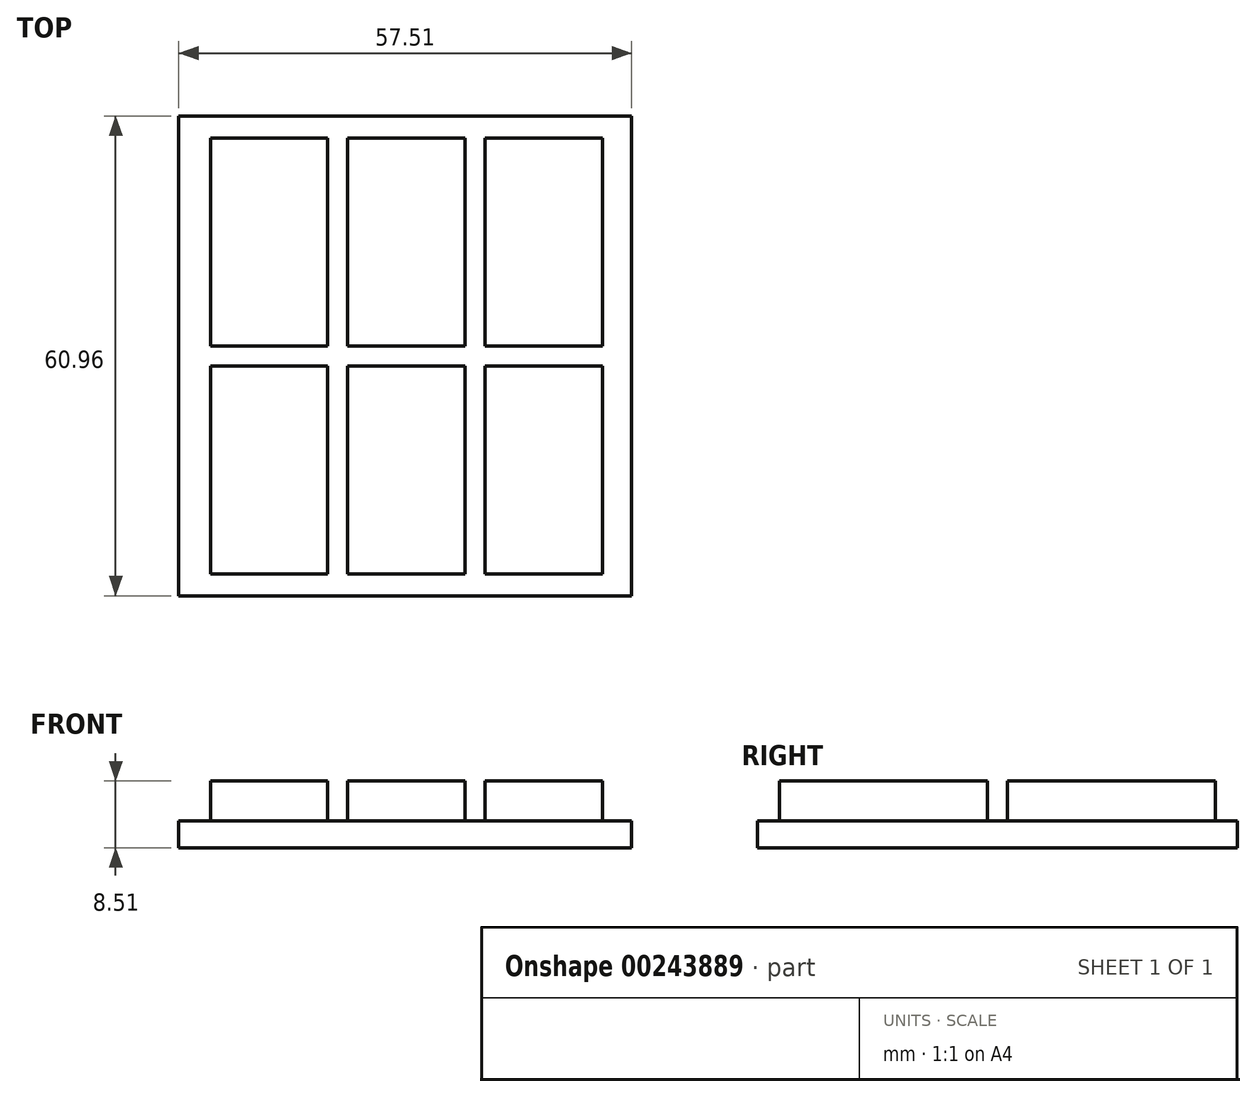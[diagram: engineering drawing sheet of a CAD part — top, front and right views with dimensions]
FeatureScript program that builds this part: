
annotation { "Feature Type Name" : "Feature", "Feature Type Description" : "" }
export const myFeature = defineFeature(function(context is Context, id is Id, definition is map)
    precondition{}
    {
        {
            var Q0;
            Q0=qCreatedBy(makeId("Top.planeOp"),FACE);
            var sketch = newSketch(context, id + "F0", { "sketchPlane" : qUnion([Q0])});
            skLineSegment(sketch, "E0.bottom", {"start": v(-24.89, 27.69) * mm, "end": v(-9.99, 27.69) * mm});
            skLineSegment(sketch, "E0.top", {"start": v(-24.89, 1.27) * mm, "end": v(-9.99, 1.27) * mm});
            skLineSegment(sketch, "E0.left", {"start": v(-24.89, 27.69) * mm, "end": v(-24.89, 1.27) * mm});
            skLineSegment(sketch, "E0.right", {"start": v(-9.99, 27.69) * mm, "end": v(-9.99, 1.27) * mm});
            skLineSegment(sketch, "E1.0.1.0", {"start": v(-9.99, -1.27) * mm, "end": v(-9.99, -27.69) * mm});
            skLineSegment(sketch, "E1.0.1.1", {"start": v(-24.89, -1.27) * mm, "end": v(-24.89, -27.69) * mm});
            skLineSegment(sketch, "E1.0.1.2", {"start": v(-24.89, -27.69) * mm, "end": v(-9.99, -27.69) * mm});
            skLineSegment(sketch, "E1.0.1.3", {"start": v(-24.89, -1.27) * mm, "end": v(-9.99, -1.27) * mm});
            skLineSegment(sketch, "E1.1.0.0", {"start": v(7.45, 27.69) * mm, "end": v(7.45, 1.27) * mm});
            skLineSegment(sketch, "E1.1.0.1", {"start": v(-7.45, 27.69) * mm, "end": v(-7.45, 1.27) * mm});
            skLineSegment(sketch, "E1.1.0.2", {"start": v(-7.45, 1.27) * mm, "end": v(7.45, 1.27) * mm});
            skLineSegment(sketch, "E1.1.0.3", {"start": v(-7.45, 27.69) * mm, "end": v(7.45, 27.69) * mm});
            skLineSegment(sketch, "E1.1.1.0", {"start": v(7.45, -1.27) * mm, "end": v(7.45, -27.69) * mm});
            skLineSegment(sketch, "E1.1.1.1", {"start": v(-7.45, -1.27) * mm, "end": v(-7.45, -27.69) * mm});
            skLineSegment(sketch, "E1.1.1.2", {"start": v(-7.45, -27.69) * mm, "end": v(7.45, -27.69) * mm});
            skLineSegment(sketch, "E1.1.1.3", {"start": v(-7.45, -1.27) * mm, "end": v(7.45, -1.27) * mm});
            skLineSegment(sketch, "E1.2.0.0", {"start": v(24.89, 27.69) * mm, "end": v(24.89, 1.27) * mm});
            skLineSegment(sketch, "E1.2.0.1", {"start": v(9.99, 27.69) * mm, "end": v(9.99, 1.27) * mm});
            skLineSegment(sketch, "E1.2.0.2", {"start": v(9.99, 1.27) * mm, "end": v(24.89, 1.27) * mm});
            skLineSegment(sketch, "E1.2.0.3", {"start": v(9.99, 27.69) * mm, "end": v(24.89, 27.69) * mm});
            skLineSegment(sketch, "E1.2.1.0", {"start": v(24.89, -1.27) * mm, "end": v(24.89, -27.69) * mm});
            skLineSegment(sketch, "E1.2.1.1", {"start": v(9.99, -1.27) * mm, "end": v(9.99, -27.69) * mm});
            skLineSegment(sketch, "E1.2.1.2", {"start": v(9.99, -27.69) * mm, "end": v(24.89, -27.69) * mm});
            skLineSegment(sketch, "E1.2.1.3", {"start": v(9.99, -1.27) * mm, "end": v(24.89, -1.27) * mm});
            skLineSegment(sketch, "E1.direction1", {"start": v(-24.89, 1.27) * mm, "end": v(-7.45, 1.27) * mm, "construction": true});
            skLineSegment(sketch, "E1.direction2", {"start": v(-24.89, 1.27) * mm, "end": v(-24.89, -27.69) * mm, "construction": true});
            skSolve(sketch);
        }
        {
            var Q0;
            Q0=makeQuery(id+"F0.imprint","IMPRINT",FACE,{"disambiguationData":[TD([[makeQuery(id+"F0.imprint","IMPRINT",EDGE,{"derivedFrom":sQuery(id+"F0.wireOp",EDGE,"E0.bottom")}),-1.0]])]});
            var Q1;
            Q1=makeQuery(id+"F0.imprint","IMPRINT",FACE,{"disambiguationData":[TD([[makeQuery(id+"F0.imprint","IMPRINT",EDGE,{"derivedFrom":sQuery(id+"F0.wireOp",EDGE,"E1.1.0.0")}),-1.0]])]});
            var Q2;
            Q2=makeQuery(id+"F0.imprint","IMPRINT",FACE,{"disambiguationData":[TD([[makeQuery(id+"F0.imprint","IMPRINT",EDGE,{"derivedFrom":sQuery(id+"F0.wireOp",EDGE,"E1.2.0.0")}),-1.0]])]});
            var Q3;
            Q3=makeQuery(id+"F0.imprint","IMPRINT",FACE,{"disambiguationData":[TD([[makeQuery(id+"F0.imprint","IMPRINT",EDGE,{"derivedFrom":sQuery(id+"F0.wireOp",EDGE,"E1.2.1.0")}),-1.0]])]});
            var Q4;
            Q4=makeQuery(id+"F0.imprint","IMPRINT",FACE,{"disambiguationData":[TD([[makeQuery(id+"F0.imprint","IMPRINT",EDGE,{"derivedFrom":sQuery(id+"F0.wireOp",EDGE,"E1.1.1.0")}),-1.0]])]});
            var Q5;
            Q5=makeQuery(id+"F0.imprint","IMPRINT",FACE,{"disambiguationData":[TD([[makeQuery(id+"F0.imprint","IMPRINT",EDGE,{"derivedFrom":sQuery(id+"F0.wireOp",EDGE,"E1.0.1.0")}),-1.0]])]});
            extrude(context, id + "F1", {"entities" : qUnion([Q0, Q1, Q2, Q3, Q4, Q5]), "depth" : 5.08 * mm});
        }
        {
            var Q0;
            Q0=qCreatedBy(makeId("Front.planeOp"),FACE);
            var sketch = newSketch(context, id + "F2", { "sketchPlane" : qUnion([Q0])});
            skLineSegment(sketch, "E2.bottom", {"start": v(-28.9, 0) * mm, "end": v(28.6, 0) * mm});
            skLineSegment(sketch, "E2.top", {"start": v(-28.9, -3.43) * mm, "end": v(28.6, -3.43) * mm});
            skLineSegment(sketch, "E2.left", {"start": v(-28.9, 0) * mm, "end": v(-28.9, -3.43) * mm});
            skLineSegment(sketch, "E2.right", {"start": v(28.6, 0) * mm, "end": v(28.6, -3.43) * mm});
            skSolve(sketch);
        }
        {
            var Q0;
            Q0=makeQuery(id+"F2.imprint","IMPRINT",FACE,{"disambiguationData":[TD([[makeQuery(id+"F2.imprint","IMPRINT",EDGE,{"derivedFrom":sQuery(id+"F2.wireOp",EDGE,"E2.bottom")}),-1.0]])]});
            extrude(context, id + "F3", {"entities" : qUnion([Q0]), "endBound" : BoundingType.SYMMETRIC, "depth" : 60.96 * mm});
        }
    });
